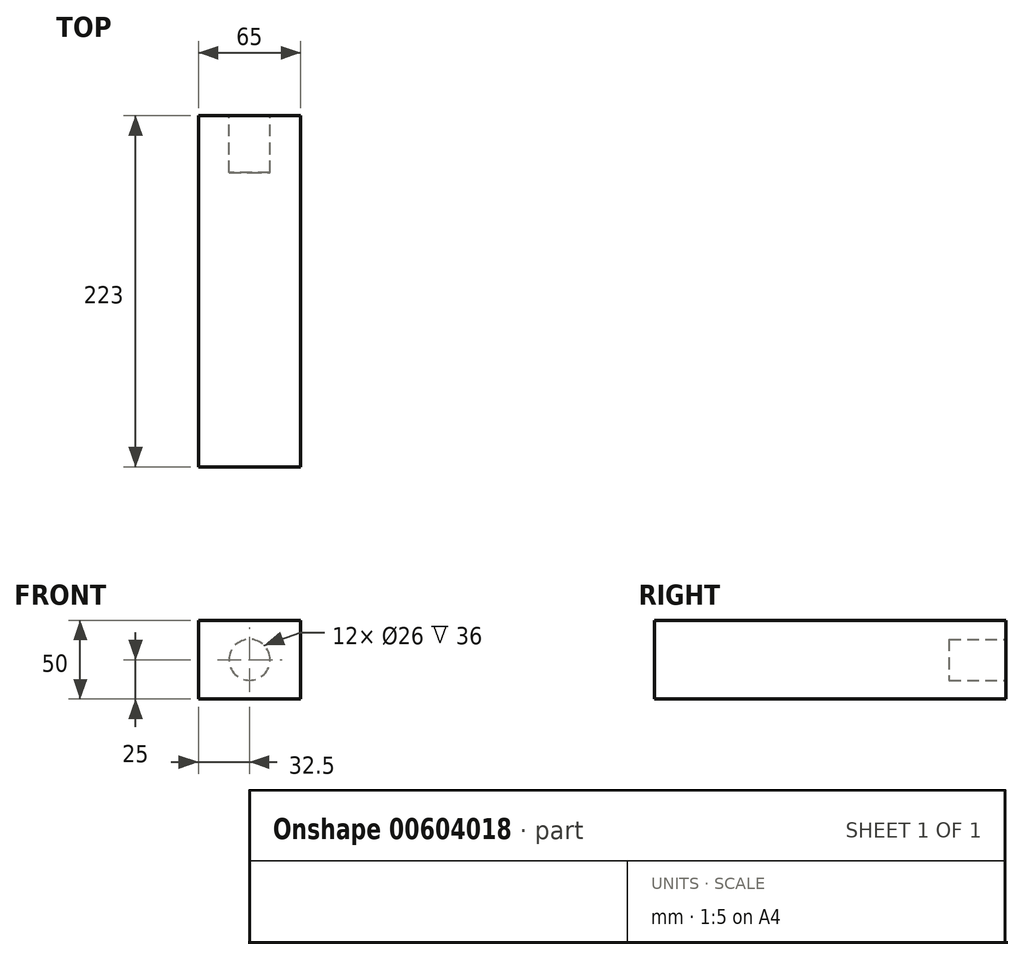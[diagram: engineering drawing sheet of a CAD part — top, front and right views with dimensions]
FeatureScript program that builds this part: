
annotation { "Feature Type Name" : "Feature", "Feature Type Description" : "" }
export const myFeature = defineFeature(function(context is Context, id is Id, definition is map)
    precondition{}
    {
        {
            var Q0;
            Q0=qCreatedBy(makeId("Front.planeOp"),FACE);
            var sketch = newSketch(context, id + "F0", { "sketchPlane" : qUnion([Q0])});
            skLineSegment(sketch, "E0", {"start": v(-32.5, 25) * mm, "end": v(-32.5, -25) * mm});
            skLineSegment(sketch, "E1", {"start": v(-32.5, -25) * mm, "end": v(32.5, -25) * mm});
            skLineSegment(sketch, "E2", {"start": v(32.5, -25) * mm, "end": v(32.5, 25) * mm});
            skLineSegment(sketch, "E3", {"start": v(32.5, 25) * mm, "end": v(-32.5, 25) * mm});
            skLineSegment(sketch, "E4", {"start": v(0, 0) * mm, "end": v(0, 25) * mm, "construction": true});
            skLineSegment(sketch, "E5", {"start": v(0, 0) * mm, "end": v(32.5, 0) * mm, "construction": true});
            skSolve(sketch);
        }
        {
            var Q0;
            Q0=makeQuery(id+"F0.imprint","IMPRINT",FACE,{"disambiguationData":[TD([[makeQuery(id+"F0.imprint","IMPRINT",EDGE,{"derivedFrom":sQuery(id+"F0.wireOp",EDGE,"E0")}),1.0]])]});
            extrude(context, id + "F1", {"entities" : qUnion([Q0]), "depth" : 223 * mm, "offsetDistance" : 25 * mm});
        }
        {
            var Q0;
            Q0=makeQuery(id+"F1.opExtrude","SWEPT_FACE",FACE,{"disambiguationData":[OSD([sQuery(id+"F0.wireOp",EDGE,"E2")])]});
            var sketch = newSketch(context, id + "F2", { "sketchPlane" : qUnion([Q0])});
            skArc(sketch, "E6", {"start": v(-85.47, 25) * mm, "mid": v(-158.52, 11.77) * mm, "end": v(-223, -25) * mm});
            skLineSegment(sketch, "E7", {"start": v(-85.47, 25) * mm, "end": v(-223, 25) * mm});
            skLineSegment(sketch, "E8", {"start": v(-223, 25) * mm, "end": v(-223, -25) * mm});
            skSolve(sketch);
        }
        {
            var Q0;
            Q0=makeQuery(id+"F1.opExtrude","CAP_FACE",FACE,{"disambiguationData":[OSD([sQuery(id+"F0.wireOp",EDGE,"E0"),sQuery(id+"F0.wireOp",EDGE,"E1"),sQuery(id+"F0.wireOp",EDGE,"E2"),sQuery(id+"F0.wireOp",EDGE,"E3")])],"isStart":true});
            var sketch = newSketch(context, id + "F3", { "sketchPlane" : qUnion([Q0])});
            skCircle(sketch, "E9", {"center": v(0, 0) * mm, "radius": 13 * mm});
            skLineSegment(sketch, "E10", {"start": v(0, -13) * mm, "end": v(0, -25) * mm, "construction": true});
            skSolve(sketch);
        }
        {
            var Q0;
            Q0 = qSketchRegion(id + "F3", true);
            extrude(context, id + "F4", {"entities" : qUnion([Q0]), "operationType" : NewBodyOperationType.REMOVE, "oppositeDirection" : true, "depth" : 36 * mm, "offsetDistance" : 25 * mm});
        }
    });
